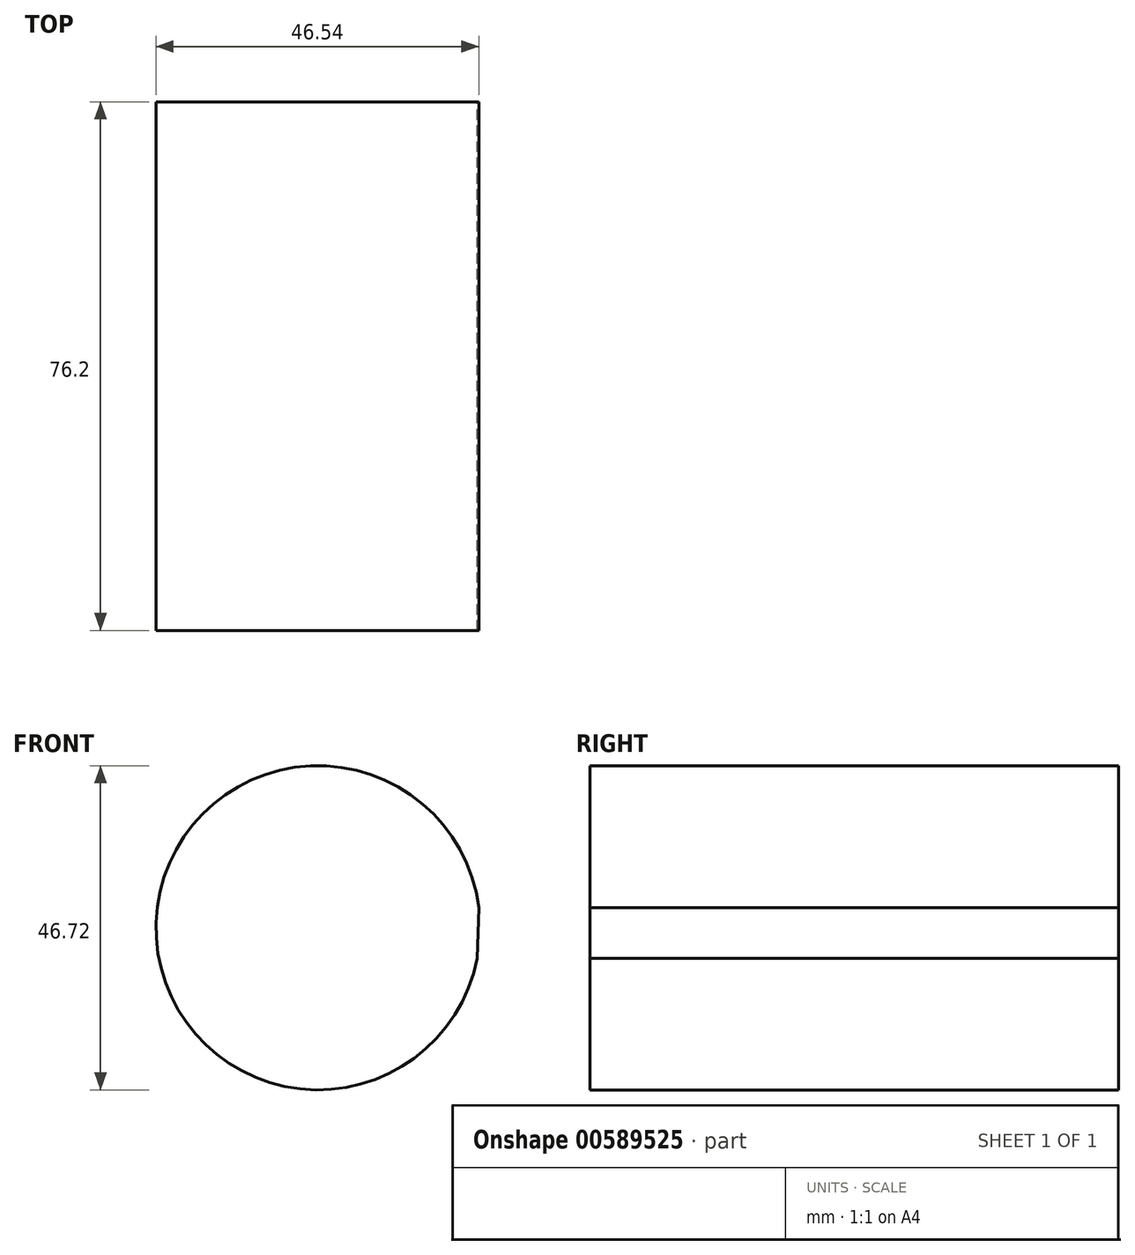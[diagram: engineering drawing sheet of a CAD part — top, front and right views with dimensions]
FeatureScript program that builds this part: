
annotation { "Feature Type Name" : "Feature", "Feature Type Description" : "" }
export const myFeature = defineFeature(function(context is Context, id is Id, definition is map)
    precondition{}
    {
        {
            var Q0;
            Q0=qCreatedBy(makeId("Front.planeOp"),FACE);
            var sketch = newSketch(context, id + "F0", { "sketchPlane" : qUnion([Q0])});
            skLineSegment(sketch, "E0.bottom", {"start": v(-141.52, 47.06) * mm, "end": v(-81.1, 47.06) * mm});
            skLineSegment(sketch, "E0.top", {"start": v(-141.52, 18.16) * mm, "end": v(-81.1, 18.16) * mm});
            skLineSegment(sketch, "E0.left", {"start": v(-141.52, 47.06) * mm, "end": v(-141.52, 18.16) * mm});
            skLineSegment(sketch, "E0.right", {"start": v(-81.1, 47.06) * mm, "end": v(-81.1, 18.16) * mm});
            skCircle(sketch, "E1", {"center": v(-105.47, -21.33) * mm, "radius": 23.36 * mm});
            skFitSpline(sketch, "E2", {"points": [v(-141.52, 18.16) * mm, v(-128.41, -25.7) * mm], "startDerivative": vector(13.12, -43.86) * mm, "endDerivative": vector(13.12, -43.86) * mm});
            skFitSpline(sketch, "E3", {"points": [v(-81.1, 18.16) * mm, v(-82.52, -25.7) * mm], "startDerivative": vector(-1.43, -43.86) * mm, "endDerivative": vector(-1.43, -43.86) * mm});
            skSolve(sketch);
        }
        {
            var Q0;
            {var subQ0=sQuery(id+"F0.wireOp",EDGE,"E1");var subQ1=makeQuery(id+"F0.imprint","INTERSECT",VERTEX,{"derivedFrom":[subQ0,sQuery(id+"F0.wireOp",EDGE,"E2")]});Q0=makeQuery(id+"F0.imprint","IMPRINT",FACE,{"disambiguationData":[TD([[makeQuery(id+"F0.imprint","IMPRINT",EDGE,{"disambiguationData":[TD([[subQ1,1.0]])],"derivedFrom":subQ0}),1.0]])]});}
            extrude(context, id + "F1", {"entities" : qUnion([Q0]), "depth" : 76.2 * mm, "offsetDistance" : 25.4 * mm});
        }
    });
